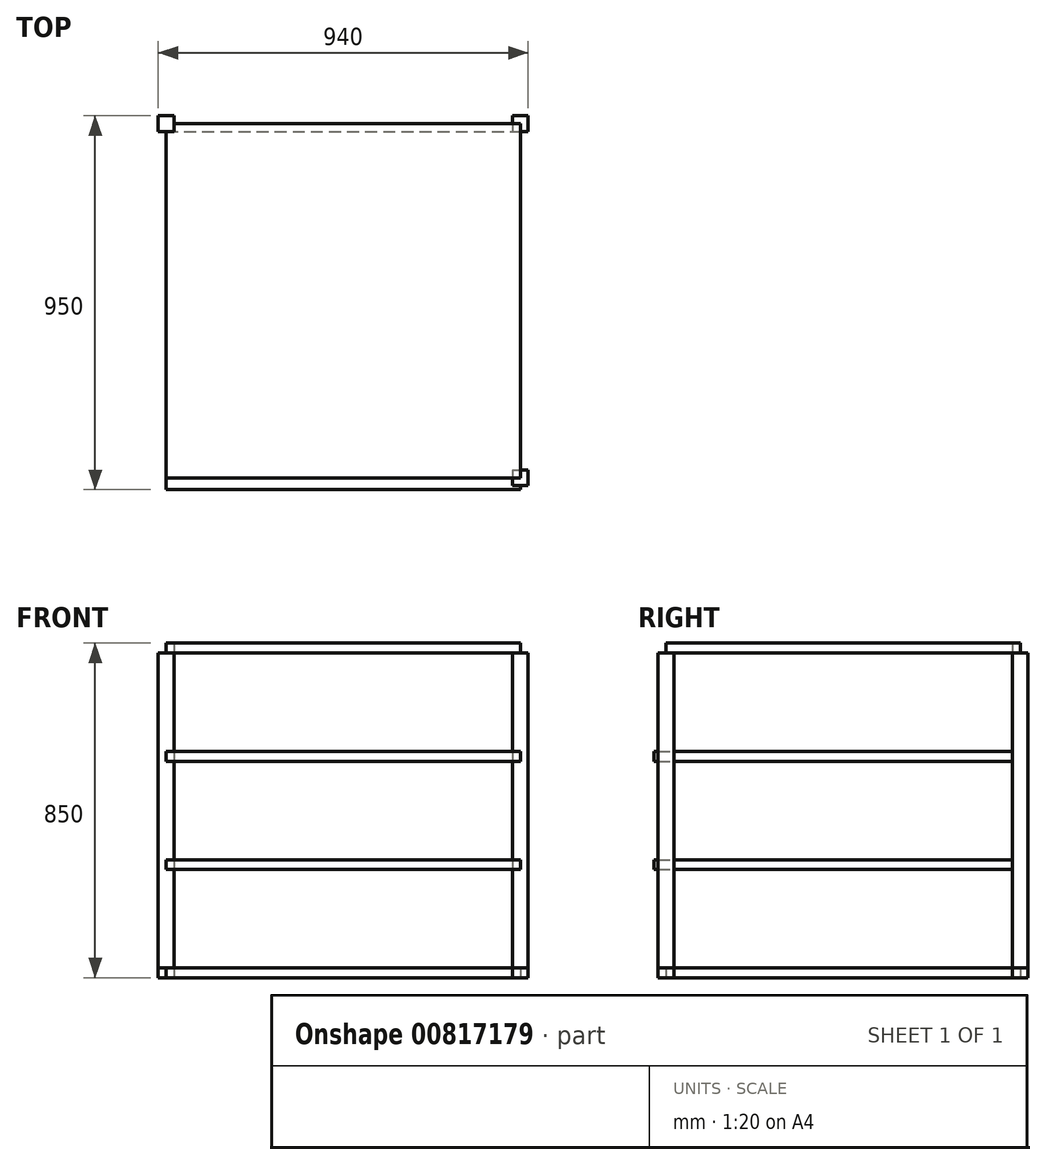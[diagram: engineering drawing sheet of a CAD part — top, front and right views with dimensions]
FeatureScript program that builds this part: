
annotation { "Feature Type Name" : "Feature", "Feature Type Description" : "" }
export const myFeature = defineFeature(function(context is Context, id is Id, definition is map)
    precondition{}
    {
        {
            var Q0;
            Q0=qCreatedBy(makeId("Top.planeOp"),FACE);
            var sketch = newSketch(context, id + "F0", { "sketchPlane" : qUnion([Q0])});
            skLineSegment(sketch, "E0.bottom", {"start": v(-450, 450) * mm, "end": v(450, 450) * mm});
            skLineSegment(sketch, "E0.top", {"start": v(-450, -450) * mm, "end": v(450, -450) * mm});
            skLineSegment(sketch, "E0.left", {"start": v(-450, 450) * mm, "end": v(-450, -450) * mm});
            skLineSegment(sketch, "E0.right", {"start": v(450, 450) * mm, "end": v(450, -450) * mm});
            skPoint(sketch, "E0.middle", {"position": v(0, 0) * mm});
            skLineSegment(sketch, "E1.bottom", {"start": v(-430, 470) * mm, "end": v(-470, 470) * mm});
            skLineSegment(sketch, "E1.top", {"start": v(-430, 430) * mm, "end": v(-470, 430) * mm});
            skLineSegment(sketch, "E1.left", {"start": v(-430, 470) * mm, "end": v(-430, 430) * mm});
            skLineSegment(sketch, "E1.right", {"start": v(-470, 470) * mm, "end": v(-470, 430) * mm});
            skPoint(sketch, "E1.middle", {"position": v(-450, 450) * mm});
            skLineSegment(sketch, "E2.bottom", {"start": v(430, 470) * mm, "end": v(470, 470) * mm});
            skLineSegment(sketch, "E2.top", {"start": v(430, 430) * mm, "end": v(470, 430) * mm});
            skLineSegment(sketch, "E2.left", {"start": v(430, 470) * mm, "end": v(430, 430) * mm});
            skLineSegment(sketch, "E2.right", {"start": v(470, 470) * mm, "end": v(470, 430) * mm});
            skPoint(sketch, "E2.middle", {"position": v(450, 450) * mm});
            skLineSegment(sketch, "E3.bottom", {"start": v(430, -430) * mm, "end": v(470, -430) * mm});
            skLineSegment(sketch, "E3.top", {"start": v(430, -470) * mm, "end": v(470, -470) * mm});
            skLineSegment(sketch, "E3.left", {"start": v(430, -430) * mm, "end": v(430, -470) * mm});
            skLineSegment(sketch, "E3.right", {"start": v(470, -430) * mm, "end": v(470, -470) * mm});
            skPoint(sketch, "E3.middle", {"position": v(450, -450) * mm});
            skSolve(sketch);
        }
        {
            var Q0;
            {var subQ6=sQuery(id+"F0.wireOp",EDGE,"E2.bottom");Q0=makeQuery(id+"F0.imprint","IMPRINT",FACE,{"disambiguationData":[TD([[makeQuery(id+"F0.imprint","IMPRINT",EDGE,{"derivedFrom":subQ6}),-1.0]])]});}
            var Q1;
            {var subQ0=sQuery(id+"F0.wireOp",EDGE,"E0.right");var subQ1=sQuery(id+"F0.wireOp",EDGE,"E0.bottom");var subQ2=makeQuery(id+"F0.imprint","INTERSECT",VERTEX,{"derivedFrom":[subQ1,subQ0]});Q1=makeQuery(id+"F0.imprint","IMPRINT",FACE,{"disambiguationData":[TD([[makeQuery(id+"F0.imprint","IMPRINT",EDGE,{"disambiguationData":[TD([[subQ2,1.0]])],"derivedFrom":subQ1}),-1.0]])]});}
            var Q2;
            {var subQ4=sQuery(id+"F0.wireOp",EDGE,"E1.bottom");Q2=makeQuery(id+"F0.imprint","IMPRINT",FACE,{"disambiguationData":[TD([[makeQuery(id+"F0.imprint","IMPRINT",EDGE,{"derivedFrom":subQ4}),1.0]])]});}
            var Q3;
            {var subQ0=sQuery(id+"F0.wireOp",EDGE,"E0.left");var subQ1=sQuery(id+"F0.wireOp",EDGE,"E0.bottom");var subQ2=makeQuery(id+"F0.imprint","INTERSECT",VERTEX,{"derivedFrom":[subQ1,subQ0]});Q3=makeQuery(id+"F0.imprint","IMPRINT",FACE,{"disambiguationData":[TD([[makeQuery(id+"F0.imprint","IMPRINT",EDGE,{"disambiguationData":[TD([[subQ2,-1.0]])],"derivedFrom":subQ1}),-1.0]])]});}
            var Q4;
            {var subQ4=sQuery(id+"F0.wireOp",EDGE,"E3.top");Q4=makeQuery(id+"F0.imprint","IMPRINT",FACE,{"disambiguationData":[TD([[makeQuery(id+"F0.imprint","IMPRINT",EDGE,{"derivedFrom":subQ4}),1.0]])]});}
            var Q5;
            {var subQ0=sQuery(id+"F0.wireOp",EDGE,"E0.right");var subQ1=sQuery(id+"F0.wireOp",EDGE,"E0.top");var subQ2=makeQuery(id+"F0.imprint","INTERSECT",VERTEX,{"derivedFrom":[subQ1,subQ0]});Q5=makeQuery(id+"F0.imprint","IMPRINT",FACE,{"disambiguationData":[TD([[makeQuery(id+"F0.imprint","IMPRINT",EDGE,{"disambiguationData":[TD([[subQ2,1.0]])],"derivedFrom":subQ1}),1.0]])]});}
            extrude(context, id + "F1", {"entities" : qUnion([Q0, Q1, Q2, Q3, Q4, Q5]), "depth" : 825 * mm, "offsetDistance" : 25 * mm});
        }
        {
            var Q0;
            Q0 = qSketchRegion(id + "F0", true);
            extrude(context, id + "F2", {"entities" : qUnion([Q0]), "depth" : 25 * mm, "offsetDistance" : 25 * mm});
        }
        {
            var Q0;
            Q0=makeQuery(id+"F1.opExtrude","CAP_FACE",FACE,{"disambiguationData":[OSD([sQuery(id+"F0.wireOp",EDGE,"E1.bottom"),sQuery(id+"F0.wireOp",EDGE,"E1.top"),sQuery(id+"F0.wireOp",EDGE,"E1.left"),sQuery(id+"F0.wireOp",EDGE,"E1.right")])],"isStart":false});
            var sketch = newSketch(context, id + "F3", { "sketchPlane" : qUnion([Q0])});
            skLineSegment(sketch, "E4.bottom", {"start": v(-450, 450) * mm, "end": v(450, 450) * mm});
            skLineSegment(sketch, "E4.top", {"start": v(-450, -450) * mm, "end": v(450, -450) * mm});
            skLineSegment(sketch, "E4.left", {"start": v(-450, 450) * mm, "end": v(-450, -450) * mm});
            skLineSegment(sketch, "E4.right", {"start": v(450, 450) * mm, "end": v(450, -450) * mm});
            skPoint(sketch, "E4.middle", {"position": v(0, 0) * mm});
            skPoint(sketch, "E4.cornerSnap0", {"position": v(-450, 470) * mm});
            skPoint(sketch, "E4.cornerSnap1", {"position": v(-470, 450) * mm});
            skSolve(sketch);
        }
        {
            var Q0;
            {var subQ2=sQuery(id+"F3.wireOp",EDGE,"E4.top");Q0=makeQuery(id+"F3.imprint","IMPRINT",FACE,{"disambiguationData":[TD([[makeQuery(id+"F3.imprint","IMPRINT",EDGE,{"derivedFrom":subQ2}),1.0]])]});}
            extrude(context, id + "F4", {"entities" : qUnion([Q0]), "depth" : 25 * mm, "offsetDistance" : 25 * mm});
        }
        {
            var Q0;
            Q0=makeQuery(id+"F1.opExtrude","SWEPT_FACE",FACE,{"disambiguationData":[OSD([sQuery(id+"F0.wireOp",EDGE,"E1.top")])]});
            var sketch = newSketch(context, id + "F5", { "sketchPlane" : qUnion([Q0])});
            skLineSegment(sketch, "E5.bottom", {"start": v(-450, 275) * mm, "end": v(450, 275) * mm});
            skLineSegment(sketch, "E5.top", {"start": v(-450, 300) * mm, "end": v(450, 300) * mm});
            skLineSegment(sketch, "E5.left", {"start": v(-450, 275) * mm, "end": v(-450, 300) * mm});
            skLineSegment(sketch, "E5.right", {"start": v(450, 275) * mm, "end": v(450, 300) * mm});
            skLineSegment(sketch, "E6.bottom", {"start": v(-450, 575) * mm, "end": v(450, 575) * mm});
            skLineSegment(sketch, "E6.top", {"start": v(-450, 550) * mm, "end": v(450, 550) * mm});
            skLineSegment(sketch, "E6.left", {"start": v(-450, 575) * mm, "end": v(-450, 550) * mm});
            skLineSegment(sketch, "E6.right", {"start": v(450, 575) * mm, "end": v(450, 550) * mm});
            skSolve(sketch);
        }
        {
            var Q0;
            {var subQ0=sQuery(id+"F5.wireOp",EDGE,"E6.right");Q0=makeQuery(id+"F5.imprint","IMPRINT",FACE,{"disambiguationData":[TD([[makeQuery(id+"F5.imprint","IMPRINT",EDGE,{"derivedFrom":subQ0}),-1.0]])]});}
            var Q1;
            {var subQ0=sQuery(id+"F5.wireOp",EDGE,"E5.right");Q1=makeQuery(id+"F5.imprint","IMPRINT",FACE,{"disambiguationData":[TD([[makeQuery(id+"F5.imprint","IMPRINT",EDGE,{"derivedFrom":subQ0}),1.0]])]});}
            var Q2;
            {var subQ0=sQuery(id+"F5.wireOp",EDGE,"E6.left");Q2=makeQuery(id+"F5.imprint","IMPRINT",FACE,{"disambiguationData":[TD([[makeQuery(id+"F5.imprint","IMPRINT",EDGE,{"derivedFrom":subQ0}),1.0]])]});}
            var Q3;
            {var subQ0=sQuery(id+"F5.wireOp",EDGE,"E5.left");Q3=makeQuery(id+"F5.imprint","IMPRINT",FACE,{"disambiguationData":[TD([[makeQuery(id+"F5.imprint","IMPRINT",EDGE,{"derivedFrom":subQ0}),-1.0]])]});}
            extrude(context, id + "F6", {"entities" : qUnion([Q0, Q1, Q2, Q3]), "depth" : 910 * mm, "offsetDistance" : 25 * mm});
        }
    });
